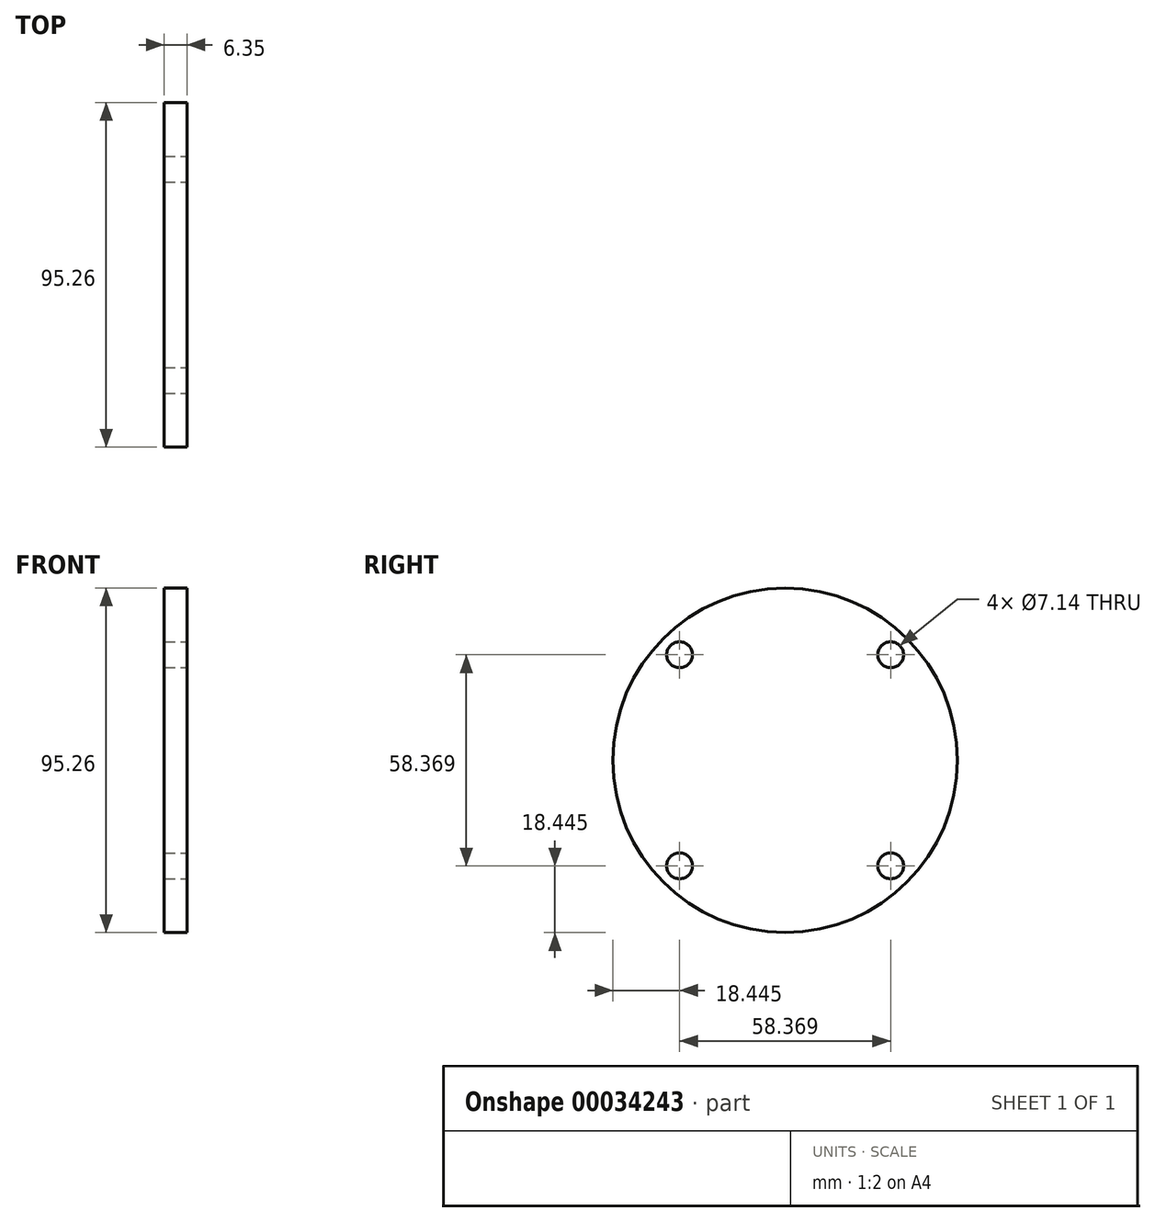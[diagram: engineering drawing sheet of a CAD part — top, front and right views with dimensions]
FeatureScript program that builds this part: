
annotation { "Feature Type Name" : "Feature", "Feature Type Description" : "" }
export const myFeature = defineFeature(function(context is Context, id is Id, definition is map)
    precondition{}
    {
        {
            var Q0;
            Q0=qCreatedBy(makeId("Right.planeOp"),FACE);
            var sketch = newSketch(context, id + "F0", { "sketchPlane" : qUnion([Q0])});
            skCircle(sketch, "E0", {"center": v(0, 0) * mm, "radius": 47.63 * mm});
            skCircle(sketch, "E1", {"center": v(29.18, 29.18) * mm, "radius": 3.57 * mm});
            skCircle(sketch, "E2", {"center": v(-29.18, 29.18) * mm, "radius": 3.57 * mm});
            skCircle(sketch, "E3", {"center": v(-29.18, -29.18) * mm, "radius": 3.57 * mm});
            skCircle(sketch, "E4", {"center": v(29.18, -29.18) * mm, "radius": 3.57 * mm});
            skSolve(sketch);
        }
        {
            var Q0;
            Q0=makeQuery(id+"F0.imprint","IMPRINT",FACE,{"disambiguationData":[TD([[makeQuery(id+"F0.imprint","IMPRINT",EDGE,{"derivedFrom":sQuery(id+"F0.wireOp",EDGE,"E0")}),1.0]])]});
            extrude(context, id + "F1", {"entities" : qUnion([Q0]), "oppositeDirection" : true, "depth" : 6.35 * mm});
        }
    });
